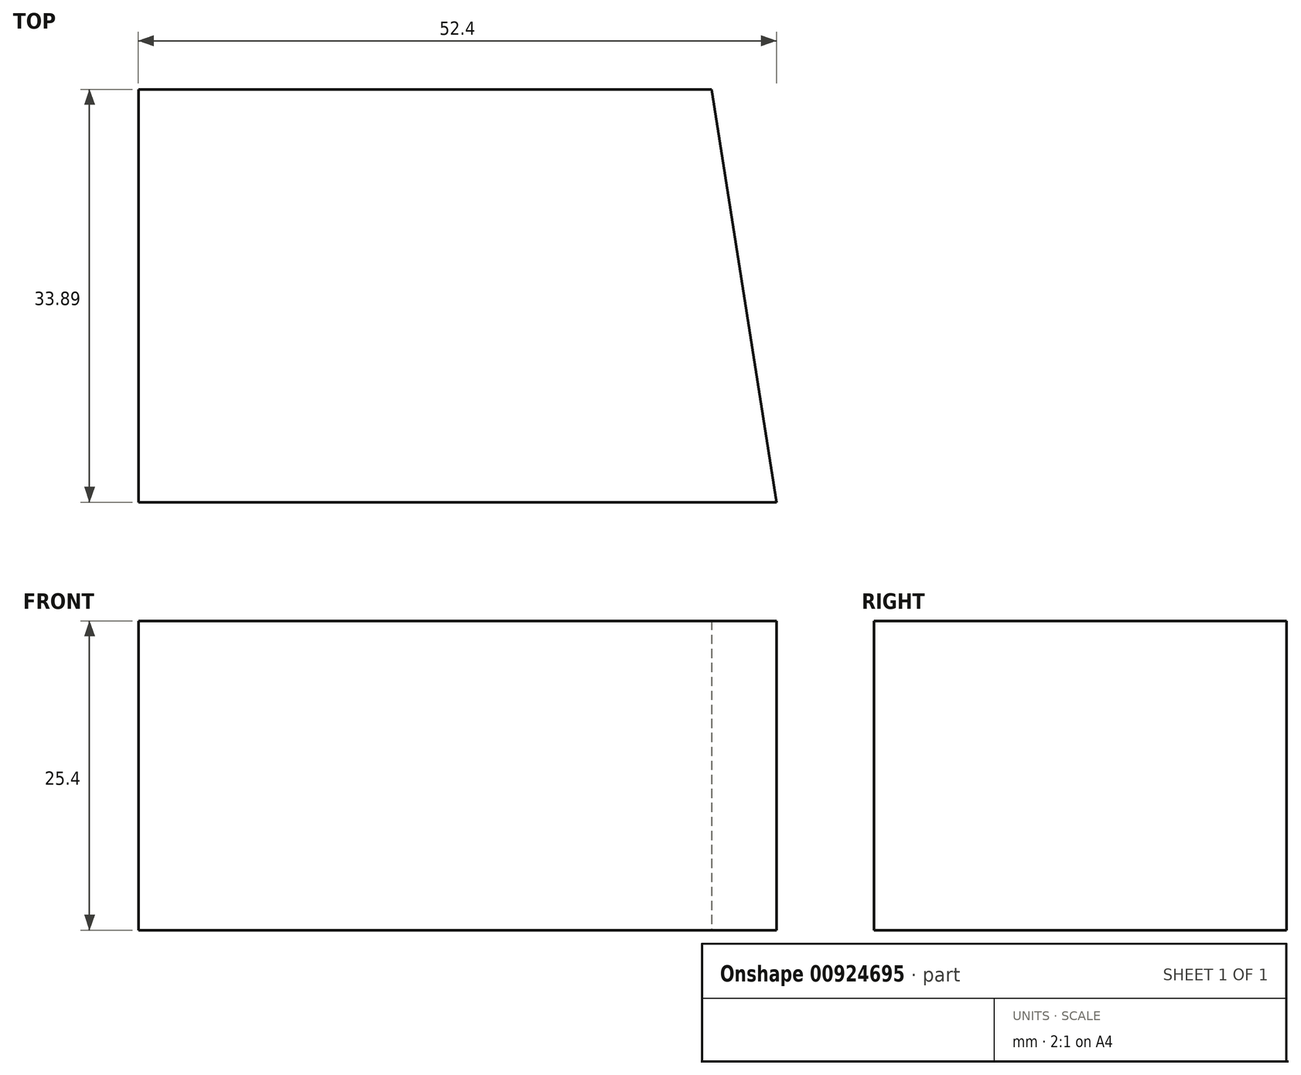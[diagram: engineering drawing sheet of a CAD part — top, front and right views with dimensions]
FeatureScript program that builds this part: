
annotation { "Feature Type Name" : "Feature", "Feature Type Description" : "" }
export const myFeature = defineFeature(function(context is Context, id is Id, definition is map)
    precondition{}
    {
        {
            var Q0;
            Q0=qCreatedBy(makeId("Top.planeOp"),FACE);
            var sketch = newSketch(context, id + "F0", { "sketchPlane" : qUnion([Q0])});
            skLineSegment(sketch, "E0", {"start": v(-21.9, 33.89) * mm, "end": v(25.18, 33.89) * mm});
            skLineSegment(sketch, "E1", {"start": v(-21.9, 33.89) * mm, "end": v(-21.9, 0) * mm});
            skLineSegment(sketch, "E2", {"start": v(-21.9, 0) * mm, "end": v(30.5, 0) * mm});
            skLineSegment(sketch, "E3", {"start": v(30.5, 0) * mm, "end": v(25.18, 33.89) * mm});
            skSolve(sketch);
        }
        {
            var Q0;
            Q0 = qSketchRegion(id + "F0", true);
            extrude(context, id + "F1", {"entities" : qUnion([Q0]), "depth" : 25.4 * mm, "offsetDistance" : 25.4 * mm});
        }
        {
            var Q0;
            Q0=makeQuery(id+"F1.opExtrude","CAP_FACE",FACE,{"disambiguationData":[OSD([sQuery(id+"F0.wireOp",EDGE,"E0"),sQuery(id+"F0.wireOp",EDGE,"E1"),sQuery(id+"F0.wireOp",EDGE,"E2"),sQuery(id+"F0.wireOp",EDGE,"E3")])],"isStart":false});
            var sketch = newSketch(context, id + "F2", { "sketchPlane" : qUnion([Q0])});
            skCircle(sketch, "E4.cCircle", {"center": v(0, 20.25) * mm, "radius": 10.5 * mm, "construction": true});
            skLineSegment(sketch, "E4.0", {"start": v(12.12, 20.3) * mm, "end": v(6.1, 9.77) * mm});
            skLineSegment(sketch, "E4.1", {"start": v(6.1, 9.77) * mm, "end": v(-6.02, 9.73) * mm});
            skLineSegment(sketch, "E4.2", {"start": v(-6.02, 9.73) * mm, "end": v(-12.12, 20.2) * mm});
            skLineSegment(sketch, "E4.3", {"start": v(-12.12, 20.2) * mm, "end": v(-6.1, 30.73) * mm});
            skLineSegment(sketch, "E4.4", {"start": v(-6.1, 30.73) * mm, "end": v(6.02, 30.77) * mm});
            skLineSegment(sketch, "E4.5", {"start": v(6.02, 30.77) * mm, "end": v(12.12, 20.3) * mm});
            skPoint(sketch, "E4.0.midPoint", {"position": v(9.11, 15.04) * mm});
            skSolve(sketch);
        }
        {
            var Q0;
            Q0=makeQuery(id+"F2.imprint","IMPRINT",FACE,{"disambiguationData":[TD([[makeQuery(id+"F2.imprint","IMPRINT",EDGE,{"derivedFrom":sQuery(id+"F2.wireOp",EDGE,"E4.0")}),-1.0]])]});
            extrude(context, id + "F3", {"entities" : qUnion([Q0]), "operationType" : NewBodyOperationType.ADD, "oppositeDirection" : true, "depth" : 25.4 * mm, "offsetDistance" : 25.4 * mm});
        }
    });
